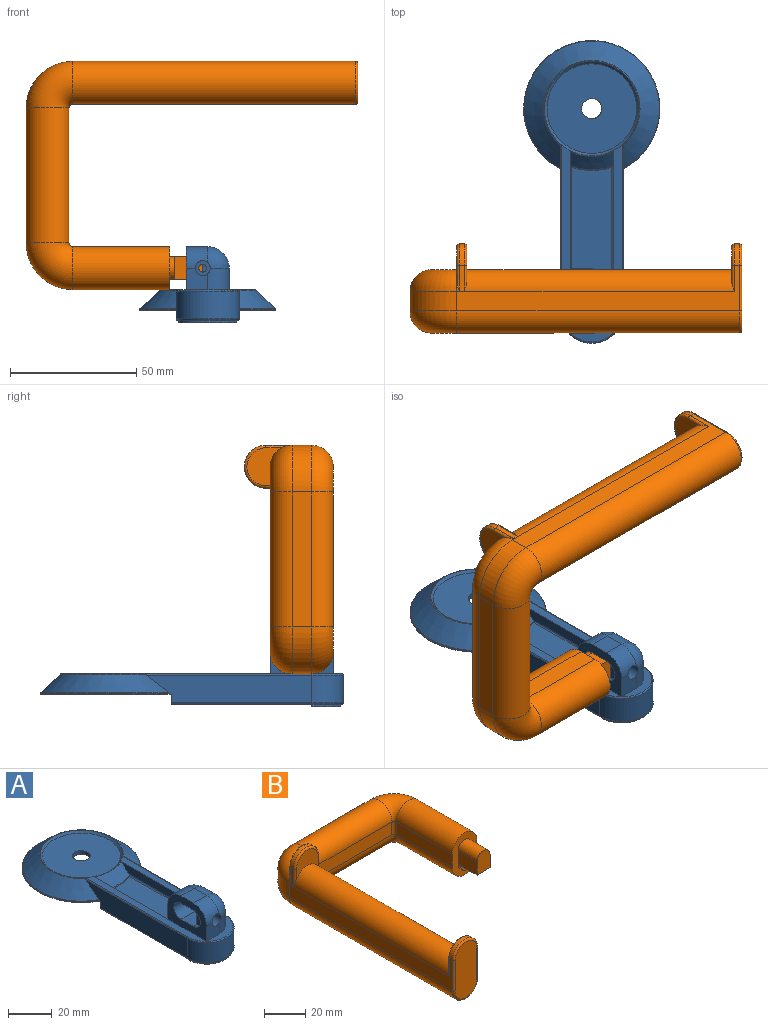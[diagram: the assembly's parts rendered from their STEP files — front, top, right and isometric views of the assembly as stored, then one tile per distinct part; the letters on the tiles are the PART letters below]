
ASSEMBLY  parts=2 mates=1
PART A: 73 faces, bbox 58.7x123.5x30.3 mm
  f0: plane 8.6x8.5mm, normal (0,-1,0), area 60.5mm2, adj f3,f34,f38,f44,f51,f58
  f1: cylinder r=1.55mm len=3.5mm, axis (0,-1,0), area 34.1mm2, adj f49,f52
  f2: plane 9x4.5mm, normal (-1,0,0), area 31.8mm2, adj f45,f49
  f3: plane 111.3x37.6mm, normal (0,0,1), area 560.3mm2, adj f0,f19,f26,f27,f29,f34,f35,f38
  f4: plane 67.48x24mm, normal (0,0,-1), area 411.5mm2, adj f16,f30,f31,f32,f53,f54,f55,f65
  f5: cylinder r=4mm len=8mm, axis (0,0,-1), area 50.3mm2, adj f8,f18
  f6: plane 43x43mm, normal (0,0,-1), area 257.6mm2, adj f7,f9
  f7: cylinder r=19.5mm len=39mm, axis (0,0,-1), area 612.6mm2, adj f6,f8
  f8: plane 39x39mm, normal (0,0,-1), area 1144.3mm2, adj f5,f7
  f9: cylinder r=21.5mm len=43mm, axis (0,0,-1), area 270.2mm2, adj f6,f11
  f10: cylinder r=23.5mm len=47mm, axis (0,0,-1), area 295.3mm2, adj f11,f17
  f11: plane 47x47mm, normal (0,0,-1), area 282.7mm2, adj f9,f10
  f12: cylinder r=12.5mm len=25mm, axis (0,0,-1), area 432mm2, adj f13,f15,f54,f58
  f13: plane 65.53x11.04mm, normal (1,0,0), area 649.8mm2, adj f12,f14,f16,f17,f20,f55,f56,f72
  f14: cylinder r=27mm len=54mm, axis (0,0,-1), area 40.7mm2, adj f13,f15,f17,f72
  f15: plane 65.53x11.04mm, normal (-1,0,0), area 649.8mm2, adj f12,f14,f16,f17,f20,f53,f59,f72
  f16: cylinder r=27.75mm len=25mm, axis (0,0,-1), area 103.5mm2, adj f4,f13,f15,f17,f53,f55
  f17: plane 54.75x54mm, normal (0,0,-1), area 574.7mm2, adj f10,f13,f14,f15,f16
  f18: plane 35.5x35.5mm, normal (0,0,1), area 939.5mm2, adj f5,f19
  f19: cone r=17.75mm half-angle=45deg, axis (0,0,1), area 162.2mm2, adj f3,f18
  f20: cone r=19mm half-angle=46.8deg, axis (0,0,-1), area 1244.9mm2, adj f13,f15,f56,f57,f59,f72
  f21: cylinder r=31.75mm len=17mm, axis (0,0,-1), area 68.8mm2, adj f22,f24,f66,f68
  f22: plane 49.91x4mm, normal (-1,0,0), area 199.6mm2, adj f21,f23,f67,f69
  f23: cylinder r=8.5mm len=17mm, axis (0,0,-1), area 146.9mm2, adj f22,f24,f30,f32,f33,f71
  f24: plane 49.91x4mm, normal (1,0,0), area 199.6mm2, adj f21,f23,f65,f70
  f25: plane 57.26x16mm, normal (0,0,-1), area 877.9mm2, adj f68,f69,f70,f71
  f26: plane 55.76x4.75mm, normal (-1,0,0), area 237.9mm2, adj f3,f29,f36,f60
  f27: plane 47.26x4.75mm, normal (1,0,0), area 199.7mm2, adj f3,f29,f37,f63
  f28: plane 45.19x16mm, normal (0,0,1), area 641.7mm2, adj f60,f61,f62,f63,f64
  f29: cone r=19mm half-angle=46.8deg, axis (0,0,-1), area 125.4mm2, adj f3,f26,f27,f60,f61,f63
  f30: plane 3x1.5mm, normal (0,1,0), area 3.1mm2, adj f4,f23,f31,f33,f67
  f31: cylinder r=11.5mm len=23mm, axis (0,0,1), area 36.1mm2, adj f4,f30,f32,f33
  f32: plane 3x1.5mm, normal (0,1,0), area 3.1mm2, adj f4,f23,f31,f33,f65
  f33: plane 23x11.5mm, normal (0,0,-1), area 94.2mm2, adj f23,f30,f31,f32
  f34: cylinder r=8.5mm len=8.6mm, axis (0,0,-1), area 113.3mm2, adj f0,f3,f35,f43,f51
  f35: plane 8.6x8mm, normal (1,0,0), area 68.8mm2, adj f3,f34,f36,f42
  f36: cylinder r=8.5mm len=13.1mm, axis (0,0,-1), area 174.9mm2, adj f26,f35,f37,f41,f62
  f37: plane 13.1x8.5mm, normal (0,1,0), area 111.4mm2, adj f27,f36,f38,f40,f64
  f38: plane 25x17.1mm, normal (-1,0,0), area 260.9mm2, adj f0,f3,f37,f39,f40,f44,f45,f46
  f39: plane 8.5x8mm, normal (0,0,1), area 68mm2, adj f38,f40,f42,f44
  f40: cylinder r=8.5mm len=8.5mm, axis (1,0,0), area 113.5mm2, adj f37,f38,f39,f41
  f41: sphere r=8.5mm, area 113.5mm2, adj f36,f40,f42
  f42: cylinder r=8.5mm len=8.5mm, axis (0,-1,0), area 106.8mm2, adj f35,f39,f41,f43
  f43: sphere r=8.5mm, area 111.9mm2, adj f34,f42,f44,f51
  f44: cylinder r=8.5mm len=8.5mm, axis (-1,0,0), area 100.7mm2, adj f0,f38,f39,f43,f51
  f45: cylinder r=4.5mm len=9mm, axis (-1,0,0), area 28.3mm2, adj f2,f38,f46,f48
  f46: plane 14x8mm, normal (0,0,-1), area 112mm2, adj f38,f45,f47,f49,f50
  f47: cylinder r=4.5mm len=14mm, axis (-1,0,0), area 197.9mm2, adj f38,f46,f48,f50
  f48: plane 14x8mm, normal (0,0,1), area 112mm2, adj f38,f45,f47,f49,f50
  f49: plane 12x9mm, normal (0,1,0), area 100.5mm2, adj f1,f2,f46,f48,f50
  f50: plane 12.5x9mm, normal (-1,0,0), area 103.8mm2, adj f46,f47,f48,f49
  f51: cylinder r=3mm len=6mm, axis (0,-1,0), area 91.4mm2, adj f0,f34,f43,f44,f52
  f52: plane 6x6mm, normal (0,-1,0), area 20.7mm2, adj f1,f51
  f53: cylinder r=0.5mm len=55.72mm, axis (0,-1,0), area 43.7mm2, adj f4,f15,f16,f54
  f54: torus R=12mm, axis (0,0,1), area 30.4mm2, adj f4,f12,f53,f55
  f55: cylinder r=0.5mm len=55.72mm, axis (0,1,0), area 43.7mm2, adj f4,f13,f16,f54
  f56: cylinder r=0.5mm len=66.03mm, axis (0,-1,0), area 51.7mm2, adj f3,f13,f20,f57,f58
  f57: torus R=18.8mm, axis (0,0,1), area 35mm2, adj f3,f20,f56,f59
  f58: torus R=12mm, axis (0,0,1), area 30.4mm2, adj f0,f3,f12,f38,f56,f59
  f59: cylinder r=0.5mm len=66.03mm, axis (0,1,0), area 51.7mm2, adj f3,f15,f20,f57,f58
  f60: cylinder r=0.5mm len=50.27mm, axis (0,1,0), area 37.5mm2, adj f26,f28,f29,f61,f62
  f61: torus R=24.53mm, axis (0,0,1), area 6.3mm2, adj f28,f29,f60,f63
  f62: torus R=9mm, axis (0,0,1), area 9.1mm2, adj f28,f36,f60,f64
  f63: cylinder r=0.5mm len=41.77mm, axis (0,-1,0), area 32.2mm2, adj f27,f28,f29,f61,f64
  f64: cylinder r=0.5mm len=8.5mm, axis (-1,0,0), area 6.5mm2, adj f28,f37,f62,f63
  f65: cylinder r=0.5mm len=50.57mm, axis (0,1,0), area 39.5mm2, adj f4,f24,f32,f66
  f66: torus R=31.25mm, axis (0,0,1), area 14mm2, adj f4,f21,f65,f67
  f67: cylinder r=0.5mm len=50.57mm, axis (0,-1,0), area 39.5mm2, adj f4,f22,f30,f66
  f68: torus R=32.25mm, axis (0,0,-1), area 13.1mm2, adj f21,f25,f69,f70
  f69: cylinder r=0.5mm len=49.91mm, axis (0,-1,0), area 38.9mm2, adj f22,f25,f68,f71
  f70: cylinder r=0.5mm len=49.91mm, axis (0,1,0), area 38.9mm2, adj f24,f25,f68,f71
  f71: torus R=8mm, axis (0,0,-1), area 20.5mm2, adj f23,f25,f69,f70
  f72: torus R=26.5mm, axis (0,0,1), area 58.6mm2, adj f13,f14,f15,f20
PART B: 50 faces, bbox 93.5x133x36.6 mm
  f0: plane 25x17mm, normal (0,-1,0), area 229.5mm2, adj f1,f2,f3,f4,f30,f31,f32,f33
  f1: cylinder r=8.5mm len=38.5mm, axis (0,1,0), area 1045.4mm2, adj f0,f2,f4,f5
  f2: plane 38.5x7.55mm, normal (1,0,0), area 290.8mm2, adj f0,f1,f3,f6
  f3: cylinder r=8.5mm len=38.5mm, axis (0,1,0), area 1045.4mm2, adj f0,f2,f4,f7
  f4: plane 38.5x7.55mm, normal (-1,0,0), area 290.6mm2, adj f0,f1,f3,f8
  f5: torus R=10mm, axis (0,0,1), area 426.5mm2, adj f1,f6,f8,f9
  f6: cylinder r=18.5mm len=18.5mm, axis (0,0,1), area 219.4mm2, adj f2,f5,f7,f10
  f7: torus R=10mm, axis (0,0,1), area 426.5mm2, adj f3,f6,f8,f11
  f8: cylinder r=1.5mm len=7.55mm, axis (0,0,1), area 17.8mm2, adj f4,f5,f7,f12
  f9: cylinder r=8.5mm len=53.5mm, axis (-1,0,0), area 1452.7mm2, adj f5,f10,f12,f13
  f10: plane 53.5x7.55mm, normal (0,1,0), area 404mm2, adj f6,f9,f11,f14
  f11: cylinder r=8.5mm len=53.5mm, axis (-1,0,0), area 1452.7mm2, adj f7,f10,f12,f15
  f12: plane 53.5x7.55mm, normal (0,-1,0), area 403.8mm2, adj f8,f9,f11,f16
  f13: torus R=10mm, axis (0,0,1), area 426.5mm2, adj f9,f14,f16,f17,f29
  f14: cylinder r=18.5mm len=18.5mm, axis (0,0,1), area 219.4mm2, adj f10,f13,f15,f18
  f15: torus R=10mm, axis (0,0,1), area 426.5mm2, adj f11,f14,f16,f19
  f16: cylinder r=1.5mm len=7.55mm, axis (0,0,1), area 17.8mm2, adj f12,f13,f15,f20
  f17: cylinder r=8.5mm len=110mm, axis (0,-1,0), area 2865.7mm2, adj f13,f18,f20,f21,f25,f27,f28,f37
  f18: plane 112x18mm, normal (-1,0,0), area 866.7mm2, adj f14,f17,f19,f23,f43,f46
  f19: cylinder r=8.5mm len=112mm, axis (0,-1,0), area 3041.3mm2, adj f15,f18,f20,f22,f45,f47
  f20: plane 109.99x7.55mm, normal (1,0,0), area 830.1mm2, adj f16,f17,f19,f45
  f21: plane 14.99x13.72mm, normal (0,1,0), area 133.5mm2, adj f17,f43,f44,f45
  f22: plane 18x2mm, normal (1,0,0), area 36mm2, adj f19,f23,f45,f49
  f23: cylinder r=8.5mm len=16.99mm, axis (0,1,0), area 53.4mm2, adj f18,f22,f44,f48
  f24: plane 33.22x15mm, normal (0,-1,0), area 449.9mm2, adj f46,f47,f48,f49
  f25: plane 10.22x2mm, normal (-1,0,0), area 20.4mm2, adj f17,f26,f39,f42
  f26: cylinder r=8.5mm len=17mm, axis (0,1,0), area 53.4mm2, adj f25,f27,f38,f41
  f27: plane 10.22x2mm, normal (1,0,0), area 20.4mm2, adj f17,f26,f37,f40
  f28: plane 15x13.72mm, normal (0,-1,0), area 133.6mm2, adj f17,f37,f38,f39
  f29: plane 15x13.72mm, normal (0,1,0), area 133.6mm2, adj f13,f40,f41,f42
  f30: plane 13x8mm, normal (-1,0,0), area 104mm2, adj f0,f31,f33,f35,f36
  f31: cylinder r=4.45mm len=8.9mm, axis (0,1,0), area 23.8mm2, adj f0,f30,f32,f34
  f32: plane 13x8mm, normal (1,0,0), area 104mm2, adj f0,f31,f33,f35,f36
  f33: cylinder r=4.45mm len=13mm, axis (0,1,0), area 181.7mm2, adj f0,f30,f32,f36
  f34: plane 8.9x4.45mm, normal (0,-1,0), area 31.1mm2, adj f31,f35
  f35: plane 11.3x8.9mm, normal (0,0,-1), area 100.6mm2, adj f30,f32,f34,f36
  f36: plane 12.45x8.9mm, normal (0,-1,0), area 102.3mm2, adj f30,f32,f33,f35
  f37: cylinder r=1mm len=10.22mm, axis (0,0,1), area 12.9mm2, adj f17,f27,f28,f38
  f38: torus R=7.5mm, axis (0,1,0), area 40.2mm2, adj f26,f28,f37,f39
  f39: cylinder r=1mm len=10.22mm, axis (0,0,-1), area 12.9mm2, adj f17,f25,f28,f38
  f40: cylinder r=1mm len=10.22mm, axis (0,0,-1), area 12.9mm2, adj f17,f27,f29,f41
  f41: torus R=7.5mm, axis (0,1,0), area 40.2mm2, adj f26,f29,f40,f42
  f42: cylinder r=1mm len=10.22mm, axis (0,0,1), area 12.9mm2, adj f17,f25,f29,f41
  f43: cylinder r=1mm len=10.45mm, axis (0,0,-1), area 13.1mm2, adj f17,f18,f21,f44
  f44: torus R=7.5mm, axis (0,-1,0), area 40.1mm2, adj f21,f23,f43,f45
  f45: cylinder r=1mm len=18mm, axis (0,0,1), area 12.8mm2, adj f17,f19,f20,f21,f22,f44
  f46: cylinder r=1mm len=18.01mm, axis (0,0,1), area 28.3mm2, adj f18,f24,f47,f48
  f47: torus R=7.5mm, axis (0,-1,0), area 40.8mm2, adj f19,f24,f46,f49
  f48: torus R=7.5mm, axis (0,-1,0), area 40.1mm2, adj f23,f24,f46,f49
  f49: cylinder r=1mm len=18.01mm, axis (0,0,-1), area 28.3mm2, adj f22,f24,f47,f48
PLACE A t=(38.68,14.16,10.67)mm
PLACE B rot(axis=(-0.58,0.58,0.58),120deg) t=(23.68,-6.76,31.27)mm
MATE pin_slot B.f1 <-> A.f40  axis (-1,0,0) through (30.18,-2.76,31.27)mm
